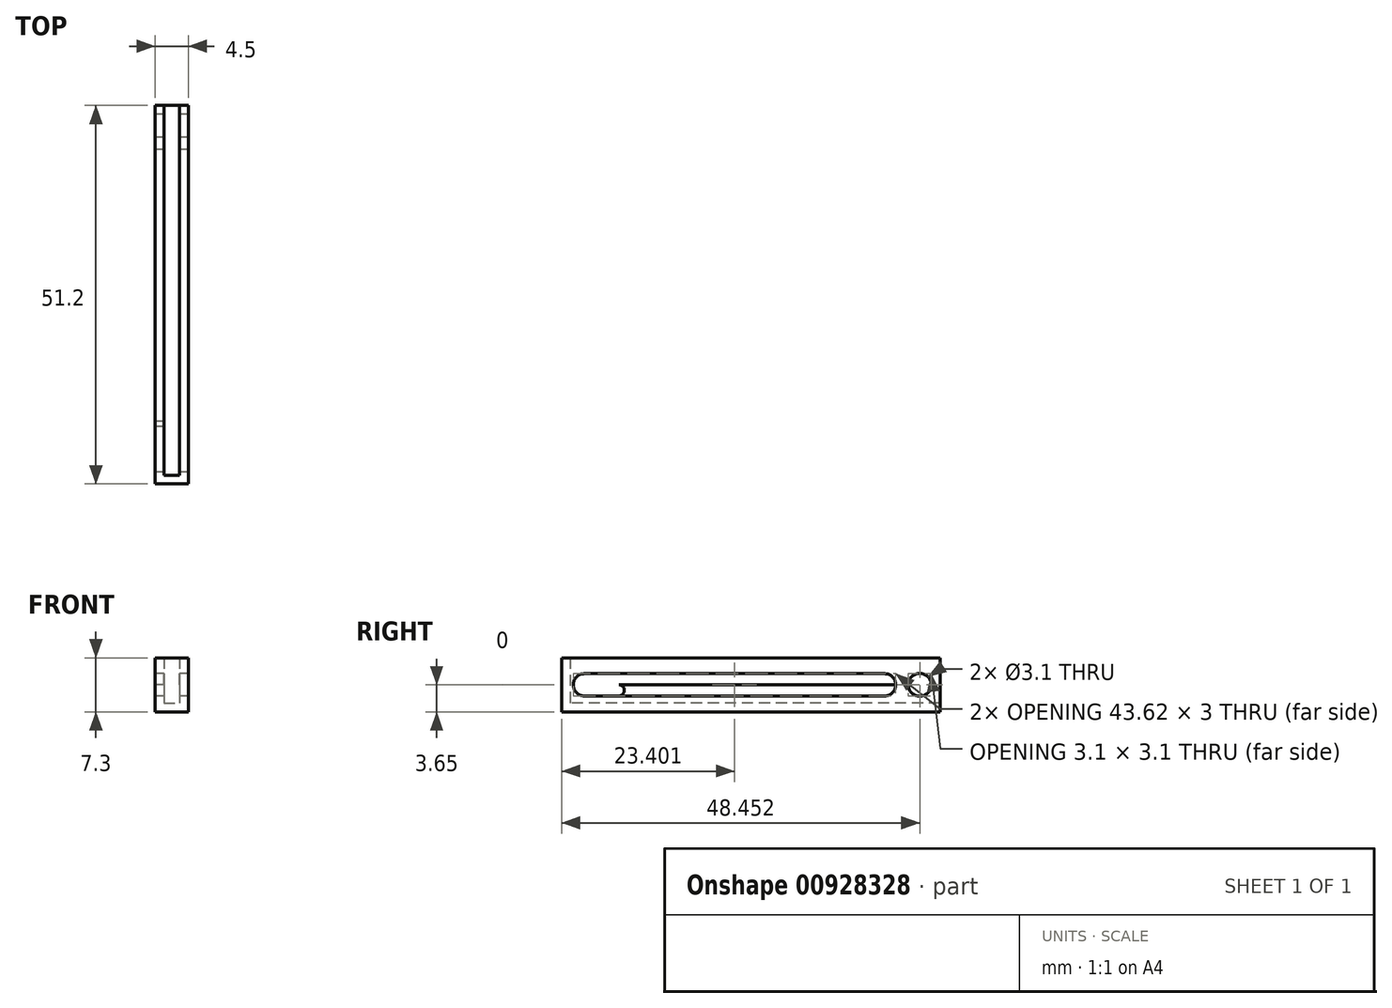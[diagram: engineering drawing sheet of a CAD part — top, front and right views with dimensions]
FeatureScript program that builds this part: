
annotation { "Feature Type Name" : "Feature", "Feature Type Description" : "" }
export const myFeature = defineFeature(function(context is Context, id is Id, definition is map)
    precondition{}
    {
        {
            var Q0;
            Q0=qCreatedBy(makeId("Top.planeOp"),FACE);
            var sketch = newSketch(context, id + "F0", { "sketchPlane" : qUnion([Q0])});
            skLineSegment(sketch, "E0.bottom", {"start": v(-5.83, 19.54) * mm, "end": v(-3.73, 19.54) * mm});
            skLineSegment(sketch, "E0.top", {"start": v(-5.83, -30.46) * mm, "end": v(-3.73, -30.46) * mm});
            skLineSegment(sketch, "E0.left", {"start": v(-5.83, 19.54) * mm, "end": v(-5.83, -30.46) * mm});
            skLineSegment(sketch, "E0.right", {"start": v(-3.73, 19.54) * mm, "end": v(-3.73, -30.46) * mm});
            skLineSegment(sketch, "E1.0", {"start": v(-7.03, 20.74) * mm, "end": v(-7.03, -31.66) * mm});
            skLineSegment(sketch, "E1.1", {"start": v(-7.03, 20.74) * mm, "end": v(-2.53, 20.74) * mm});
            skLineSegment(sketch, "E1.2", {"start": v(-2.53, 20.74) * mm, "end": v(-2.53, -31.66) * mm});
            skLineSegment(sketch, "E1.3", {"start": v(-7.03, -31.66) * mm, "end": v(-2.53, -31.66) * mm});
            skSolve(sketch);
        }
        {
            var Q0;
            Q0=makeQuery(id+"F0.imprint","IMPRINT",FACE,{"disambiguationData":[TD([[makeQuery(id+"F0.imprint","IMPRINT",EDGE,{"derivedFrom":sQuery(id+"F0.wireOp",EDGE,"E0.bottom")}),-1.0]])]});
            var Q1;
            Q1=makeQuery(id+"F0.imprint","IMPRINT",FACE,{"disambiguationData":[TD([[makeQuery(id+"F0.imprint","IMPRINT",EDGE,{"derivedFrom":sQuery(id+"F0.wireOp",EDGE,"E0.bottom")}),1.0]])]});
            extrude(context, id + "F1", {"entities" : qUnion([Q0, Q1]), "depth" : -1.2 * mm, "offsetDistance" : 25 * mm});
        }
        {
            var Q0;
            Q0=makeQuery(id+"F0.imprint","IMPRINT",FACE,{"disambiguationData":[TD([[makeQuery(id+"F0.imprint","IMPRINT",EDGE,{"derivedFrom":sQuery(id+"F0.wireOp",EDGE,"E0.bottom")}),1.0]])]});
            extrude(context, id + "F2", {"entities" : qUnion([Q0]), "operationType" : NewBodyOperationType.ADD, "depth" : 6.1 * mm, "offsetDistance" : 25 * mm});
        }
        {
            var Q0;
            {var subQ0=sQuery(id+"F0.wireOp",EDGE,"E1.1");Q0=makeQuery(id+"F2.boolean.opBoolean","MERGE",FACE,{"derivedFrom":[makeQuery(id+"F1.opExtrude","SWEPT_FACE",FACE,{"disambiguationData":[OSD([subQ0])]}),makeQuery(id+"F2.opExtrude","SWEPT_FACE",FACE,{"disambiguationData":[OSD([subQ0])]})]});}
            extrude(context, id + "F3", {"entities" : qUnion([Q0]), "operationType" : NewBodyOperationType.REMOVE, "oppositeDirection" : true, "depth" : 1.2 * mm, "offsetDistance" : 25 * mm});
        }
        {
            var Q0;
            {var subQ0=sQuery(id+"F0.wireOp",EDGE,"E1.0");Q0=makeQuery(id+"F2.boolean.opBoolean","MERGE",FACE,{"derivedFrom":[makeQuery(id+"F1.opExtrude","SWEPT_FACE",FACE,{"disambiguationData":[OSD([subQ0])]}),makeQuery(id+"F2.opExtrude","SWEPT_FACE",FACE,{"disambiguationData":[OSD([subQ0])]})]});}
            var sketch = newSketch(context, id + "F4", { "sketchPlane" : qUnion([Q0])});
            skCircle(sketch, "E2", {"center": v(-16.8, 2.45) * mm, "radius": 1.55 * mm});
            skLineSegment(sketch, "E3.bottom", {"start": v(-12.05, 3.95) * mm, "end": v(28.57, 3.95) * mm});
            skLineSegment(sketch, "E3.top", {"start": v(-12.05, 0.95) * mm, "end": v(28.57, 0.95) * mm});
            skLineSegment(sketch, "E3.left", {"start": v(-12.05, 3.95) * mm, "end": v(-12.05, 0.95) * mm});
            skLineSegment(sketch, "E3.right", {"start": v(28.57, 3.95) * mm, "end": v(28.57, 0.95) * mm});
            skLineSegment(sketch, "E4", {"start": v(-12.05, 2.45) * mm, "end": v(28.57, 2.45) * mm, "construction": true});
            skCircle(sketch, "E5", {"center": v(-12.05, 2.45) * mm, "radius": 1.5 * mm});
            skCircle(sketch, "E6", {"center": v(28.57, 2.45) * mm, "radius": 1.5 * mm});
            skSolve(sketch);
        }
        {
            var Q0;
            Q0=makeQuery(id+"F4.imprint","IMPRINT",FACE,{"disambiguationData":[TD([[makeQuery(id+"F4.imprint","IMPRINT",EDGE,{"derivedFrom":sQuery(id+"F4.wireOp",EDGE,"E2")}),1.0]])]});
            var Q1;
            Q1=makeQuery(id+"F4.imprint","IMPRINT",FACE,{"disambiguationData":[TD([[makeQuery(id+"F4.imprint","IMPRINT",EDGE,{"derivedFrom":sQuery(id+"F4.wireOp",EDGE,"E3.bottom")}),-1.0]])]});
            var Q2;
            {var subQ1=sQuery(id+"F4.wireOp",EDGE,"uFcgz5go-tB4p-AWpW-JiDX-pelhlFVr2Nxr.bottom");Q2=makeQuery(id+"F4.imprint","IMPRINT",FACE,{"disambiguationData":[TD([[makeQuery(id+"F4.imprint","IMPRINT",EDGE,{"derivedFrom":subQ1}),-1.0]])]});}
            var Q3;
            Q3=makeQuery(id+"F4.imprint","IMPRINT",FACE,{"disambiguationData":[TD([[makeQuery(id+"F4.imprint","IMPRINT",EDGE,{"derivedFrom":sQuery(id+"F4.wireOp",EDGE,"VvtEDQ9c-URMW-oA5q-UxCi-PPHgzlbXk2RG.bottom")}),-1.0]])]});
            var Q4;
            {var subQ0=sQuery(id+"F4.wireOp",EDGE,"E3.left");Q4=makeQuery(id+"F4.imprint","IMPRINT",FACE,{"disambiguationData":[TD([[makeQuery(id+"F4.imprint","IMPRINT",EDGE,{"derivedFrom":subQ0}),-1.0]])]});}
            var Q5;
            {var subQ0=sQuery(id+"F4.wireOp",EDGE,"E3.left");Q5=makeQuery(id+"F4.imprint","IMPRINT",FACE,{"disambiguationData":[TD([[makeQuery(id+"F4.imprint","IMPRINT",EDGE,{"derivedFrom":subQ0}),1.0]])]});}
            var Q6;
            {var subQ0=sQuery(id+"F4.wireOp",EDGE,"E3.right");Q6=makeQuery(id+"F4.imprint","IMPRINT",FACE,{"disambiguationData":[TD([[makeQuery(id+"F4.imprint","IMPRINT",EDGE,{"derivedFrom":subQ0}),-1.0]])]});}
            var Q7;
            {var subQ0=sQuery(id+"F4.wireOp",EDGE,"E3.right");Q7=makeQuery(id+"F4.imprint","IMPRINT",FACE,{"disambiguationData":[TD([[makeQuery(id+"F4.imprint","IMPRINT",EDGE,{"derivedFrom":subQ0}),1.0]])]});}
            extrude(context, id + "F5", {"entities" : qUnion([Q0, Q1, Q2, Q3, Q4, Q5, Q6, Q7]), "operationType" : NewBodyOperationType.REMOVE, "oppositeDirection" : true, "depth" : 25 * mm, "offsetDistance" : 25 * mm});
        }
        {
            var Q0;
            {var subQ0=sQuery(id+"F0.wireOp",EDGE,"E1.0");Q0=makeQuery(id+"F2.boolean.opBoolean","MERGE",FACE,{"derivedFrom":[makeQuery(id+"F1.opExtrude","SWEPT_FACE",FACE,{"disambiguationData":[OSD([subQ0])]}),makeQuery(id+"F2.opExtrude","SWEPT_FACE",FACE,{"disambiguationData":[OSD([subQ0])]})]});}
            var sketch = newSketch(context, id + "F6", { "sketchPlane" : qUnion([Q0])});
            skPoint(sketch, "E7.oppositeSnap0", {"position": v(-13.55, 2.45) * mm});
            skLineSegment(sketch, "E7.bottom", {"start": v(-12.05, 0.95) * mm, "end": v(23.9, 0.95) * mm});
            skLineSegment(sketch, "E7.top", {"start": v(-12.05, 2.45) * mm, "end": v(23.9, 2.45) * mm});
            skLineSegment(sketch, "E7.left", {"start": v(-12.05, 0.95) * mm, "end": v(-12.05, 2.45) * mm});
            skArc(sketch, "E8", {"start": v(23.9, 2.45) * mm, "mid": v(23.15, 1.7) * mm, "end": v(23.9, 0.95) * mm});
            skCircle(sketch, "E9", {"center": v(-12.05, 2.45) * mm, "radius": 1.5 * mm});
            skLineSegment(sketch, "E10", {"start": v(-12.05, 2.45) * mm, "end": v(-13.55, 2.45) * mm});
            skSolve(sketch);
        }
        {
            var Q0;
            Q0=makeQuery(id+"F6.imprint","IMPRINT",FACE,{"disambiguationData":[TD([[makeQuery(id+"F6.imprint","IMPRINT",EDGE,{"derivedFrom":sQuery(id+"F6.wireOp",EDGE,"INWsEHcP-EIg5-B1et-iBVi-eVKpvB2PGAZK.bottom")}),1.0]])]});
            var Q1;
            Q1=makeQuery(id+"F6.imprint","IMPRINT",FACE,{"disambiguationData":[TD([[makeQuery(id+"F6.imprint","IMPRINT",EDGE,{"derivedFrom":sQuery(id+"F6.wireOp",EDGE,"E7.bottom")}),1.0]])]});
            var Q2;
            {var subQ1=sQuery(id+"F6.wireOp",EDGE,"E7.top");var subQ3=sQuery(id+"F6.wireOp",EDGE,"E9");var subQ4=makeQuery(id+"F6.imprint","INTERSECT",VERTEX,{"derivedFrom":[subQ1,subQ3]});Q2=makeQuery(id+"F6.imprint","IMPRINT",FACE,{"disambiguationData":[TD([[makeQuery(id+"F6.imprint","IMPRINT",EDGE,{"disambiguationData":[TD([[subQ4,1.0]])],"derivedFrom":subQ3}),1.0]])]});}
            var Q3;
            {var subQ1=sQuery(id+"F6.wireOp",EDGE,"E7.left");var subQ3=sQuery(id+"F6.wireOp",EDGE,"E9");var subQ4=makeQuery(id+"F6.imprint","INTERSECT",VERTEX,{"derivedFrom":[subQ1,subQ3]});Q3=makeQuery(id+"F6.imprint","IMPRINT",FACE,{"disambiguationData":[TD([[makeQuery(id+"F6.imprint","IMPRINT",EDGE,{"disambiguationData":[TD([[subQ4,1.0]])],"derivedFrom":subQ3}),1.0]])]});}
            extrude(context, id + "F7", {"entities" : qUnion([Q0, Q1, Q2, Q3]), "operationType" : NewBodyOperationType.ADD, "depth" : -1.2 * mm, "offsetDistance" : 25 * mm});
        }
    });
